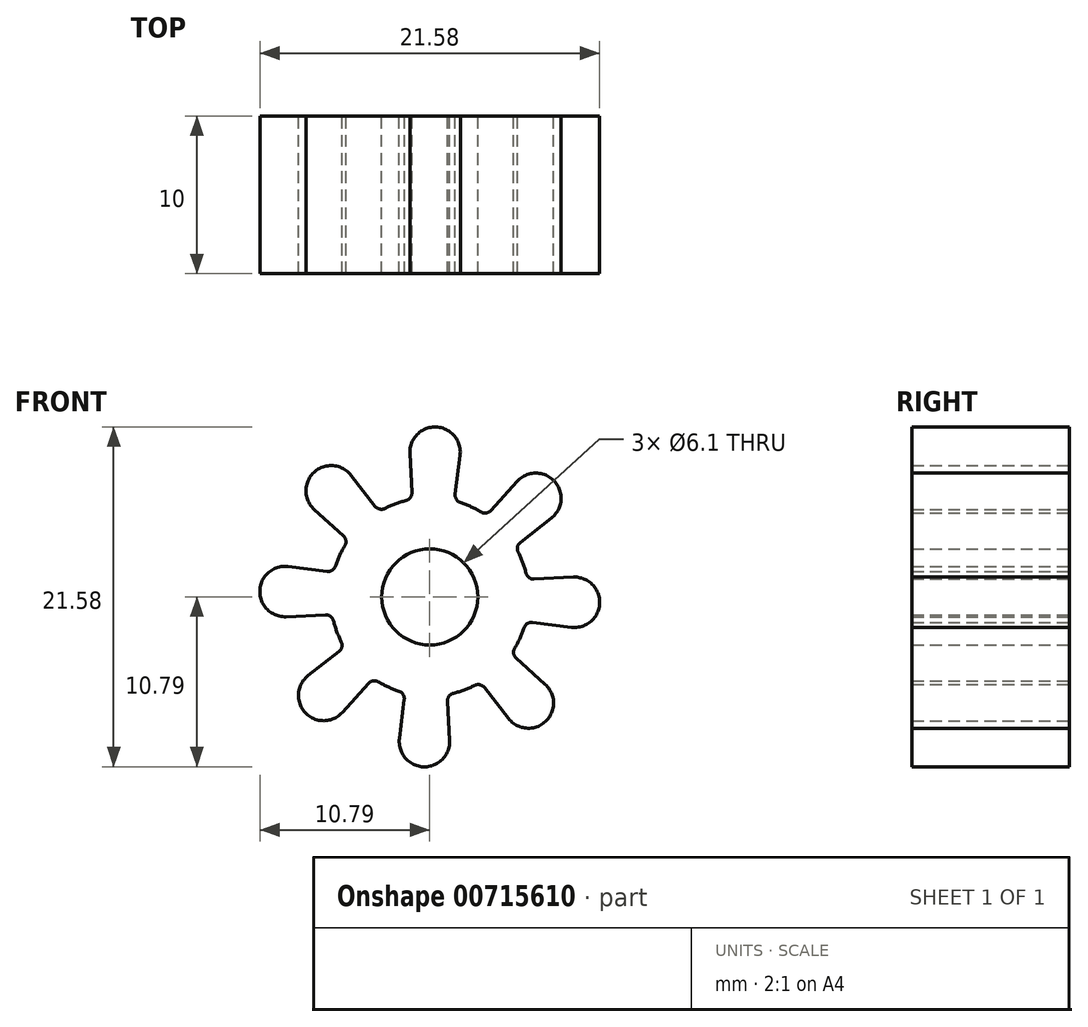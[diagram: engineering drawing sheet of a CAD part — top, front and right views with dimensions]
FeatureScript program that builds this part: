
annotation { "Feature Type Name" : "Feature", "Feature Type Description" : "" }
export const myFeature = defineFeature(function(context is Context, id is Id, definition is map)
    precondition{}
    {
        {
            var Q0;
            Q0=qCreatedBy(makeId("Front.planeOp"),FACE);
            var sketch = newSketch(context, id + "F0", { "sketchPlane" : qUnion([Q0])});
            skCircle(sketch, "E0", {"center": v(0, 0) * mm, "radius": 3.05 * mm});
            skCircle(sketch, "E1", {"center": v(0, 0) * mm, "radius": 6.3 * mm});
            skCircle(sketch, "E2", {"center": v(0, 0) * mm, "radius": 9.2 * mm, "construction": true});
            skCircle(sketch, "E3", {"center": v(0.34, 9.2) * mm, "radius": 1.6 * mm});
            skLineSegment(sketch, "E4", {"start": v(-1.26, 9.11) * mm, "end": v(-1.13, 6.63) * mm});
            skLineSegment(sketch, "E5", {"start": v(1.93, 9) * mm, "end": v(1.62, 6.52) * mm});
            skArc(sketch, "E6", {"start": v(-1.51, 6.12) * mm, "mid": v(-1.23, 6.3) * mm, "end": v(-1.13, 6.63) * mm});
            skArc(sketch, "E7", {"start": v(1.62, 6.52) * mm, "mid": v(1.7, 6.2) * mm, "end": v(1.96, 5.99) * mm});
            skArc(sketch, "E8.1.0", {"start": v(-3.47, 5.76) * mm, "mid": v(-3.18, 5.58) * mm, "end": v(-2.85, 5.62) * mm});
            skArc(sketch, "E8.1.1", {"start": v(-5.4, 3.25) * mm, "mid": v(-5.33, 3.59) * mm, "end": v(-5.49, 3.88) * mm});
            skLineSegment(sketch, "E8.1.2", {"start": v(-7.33, 5.55) * mm, "end": v(-5.49, 3.88) * mm});
            skLineSegment(sketch, "E8.1.3", {"start": v(-5, 7.72) * mm, "end": v(-3.47, 5.76) * mm});
            skCircle(sketch, "E8.1.4", {"center": v(-6.26, 6.74) * mm, "radius": 1.6 * mm});
            skArc(sketch, "E8.2.0", {"start": v(-6.52, 1.62) * mm, "mid": v(-6.2, 1.7) * mm, "end": v(-5.99, 1.96) * mm});
            skArc(sketch, "E8.2.1", {"start": v(-6.12, -1.51) * mm, "mid": v(-6.3, -1.23) * mm, "end": v(-6.63, -1.13) * mm});
            skLineSegment(sketch, "E8.2.2", {"start": v(-9.11, -1.26) * mm, "end": v(-6.63, -1.13) * mm});
            skLineSegment(sketch, "E8.2.3", {"start": v(-9, 1.93) * mm, "end": v(-6.52, 1.62) * mm});
            skCircle(sketch, "E8.2.4", {"center": v(-9.2, 0.34) * mm, "radius": 1.6 * mm});
            skArc(sketch, "E9.3.3.0", {"start": v(-5.76, -3.47) * mm, "mid": v(-5.58, -3.18) * mm, "end": v(-5.62, -2.85) * mm});
            skArc(sketch, "E9.4.3.0", {"start": v(-3.25, -5.4) * mm, "mid": v(-3.59, -5.33) * mm, "end": v(-3.88, -5.49) * mm});
            skLineSegment(sketch, "E9.8.3.0", {"start": v(-5.55, -7.33) * mm, "end": v(-3.88, -5.49) * mm});
            skLineSegment(sketch, "E9.11.3.0", {"start": v(-7.72, -5) * mm, "end": v(-5.76, -3.47) * mm});
            skCircle(sketch, "E9.14.3.0", {"center": v(-6.74, -6.26) * mm, "radius": 1.6 * mm});
            skArc(sketch, "E9.3.4.0", {"start": v(-1.62, -6.52) * mm, "mid": v(-1.7, -6.2) * mm, "end": v(-1.96, -5.99) * mm});
            skArc(sketch, "E9.4.4.0", {"start": v(1.51, -6.12) * mm, "mid": v(1.23, -6.3) * mm, "end": v(1.13, -6.63) * mm});
            skLineSegment(sketch, "E9.8.4.0", {"start": v(1.26, -9.11) * mm, "end": v(1.13, -6.63) * mm});
            skLineSegment(sketch, "E9.11.4.0", {"start": v(-1.93, -9) * mm, "end": v(-1.62, -6.52) * mm});
            skCircle(sketch, "E9.14.4.0", {"center": v(-0.34, -9.2) * mm, "radius": 1.6 * mm});
            skArc(sketch, "E9.3.5.0", {"start": v(3.47, -5.76) * mm, "mid": v(3.18, -5.58) * mm, "end": v(2.85, -5.62) * mm});
            skArc(sketch, "E9.4.5.0", {"start": v(5.4, -3.25) * mm, "mid": v(5.33, -3.59) * mm, "end": v(5.49, -3.88) * mm});
            skLineSegment(sketch, "E9.8.5.0", {"start": v(7.33, -5.55) * mm, "end": v(5.49, -3.88) * mm});
            skLineSegment(sketch, "E9.11.5.0", {"start": v(5, -7.72) * mm, "end": v(3.47, -5.76) * mm});
            skCircle(sketch, "E9.14.5.0", {"center": v(6.26, -6.74) * mm, "radius": 1.6 * mm});
            skArc(sketch, "E9.3.6.0", {"start": v(6.52, -1.62) * mm, "mid": v(6.2, -1.7) * mm, "end": v(5.99, -1.96) * mm});
            skArc(sketch, "E9.4.6.0", {"start": v(6.12, 1.51) * mm, "mid": v(6.3, 1.23) * mm, "end": v(6.63, 1.13) * mm});
            skLineSegment(sketch, "E9.8.6.0", {"start": v(9.11, 1.26) * mm, "end": v(6.63, 1.13) * mm});
            skLineSegment(sketch, "E9.11.6.0", {"start": v(9, -1.93) * mm, "end": v(6.52, -1.62) * mm});
            skCircle(sketch, "E9.14.6.0", {"center": v(9.2, -0.34) * mm, "radius": 1.6 * mm});
            skArc(sketch, "E9.3.7.0", {"start": v(5.76, 3.47) * mm, "mid": v(5.58, 3.18) * mm, "end": v(5.62, 2.85) * mm});
            skArc(sketch, "E9.4.7.0", {"start": v(3.25, 5.4) * mm, "mid": v(3.59, 5.33) * mm, "end": v(3.88, 5.49) * mm});
            skLineSegment(sketch, "E9.8.7.0", {"start": v(5.55, 7.33) * mm, "end": v(3.88, 5.49) * mm});
            skLineSegment(sketch, "E9.11.7.0", {"start": v(7.72, 5) * mm, "end": v(5.76, 3.47) * mm});
            skCircle(sketch, "E9.14.7.0", {"center": v(6.74, 6.26) * mm, "radius": 1.6 * mm});
            skSolve(sketch);
        }
        {
            var Q0;
            Q0 = qSketchRegion(id + "F0", true);
            extrude(context, id + "F1", {"entities" : qUnion([Q0]), "depth" : 10 * mm, "offsetDistance" : 25 * mm});
        }
    });
